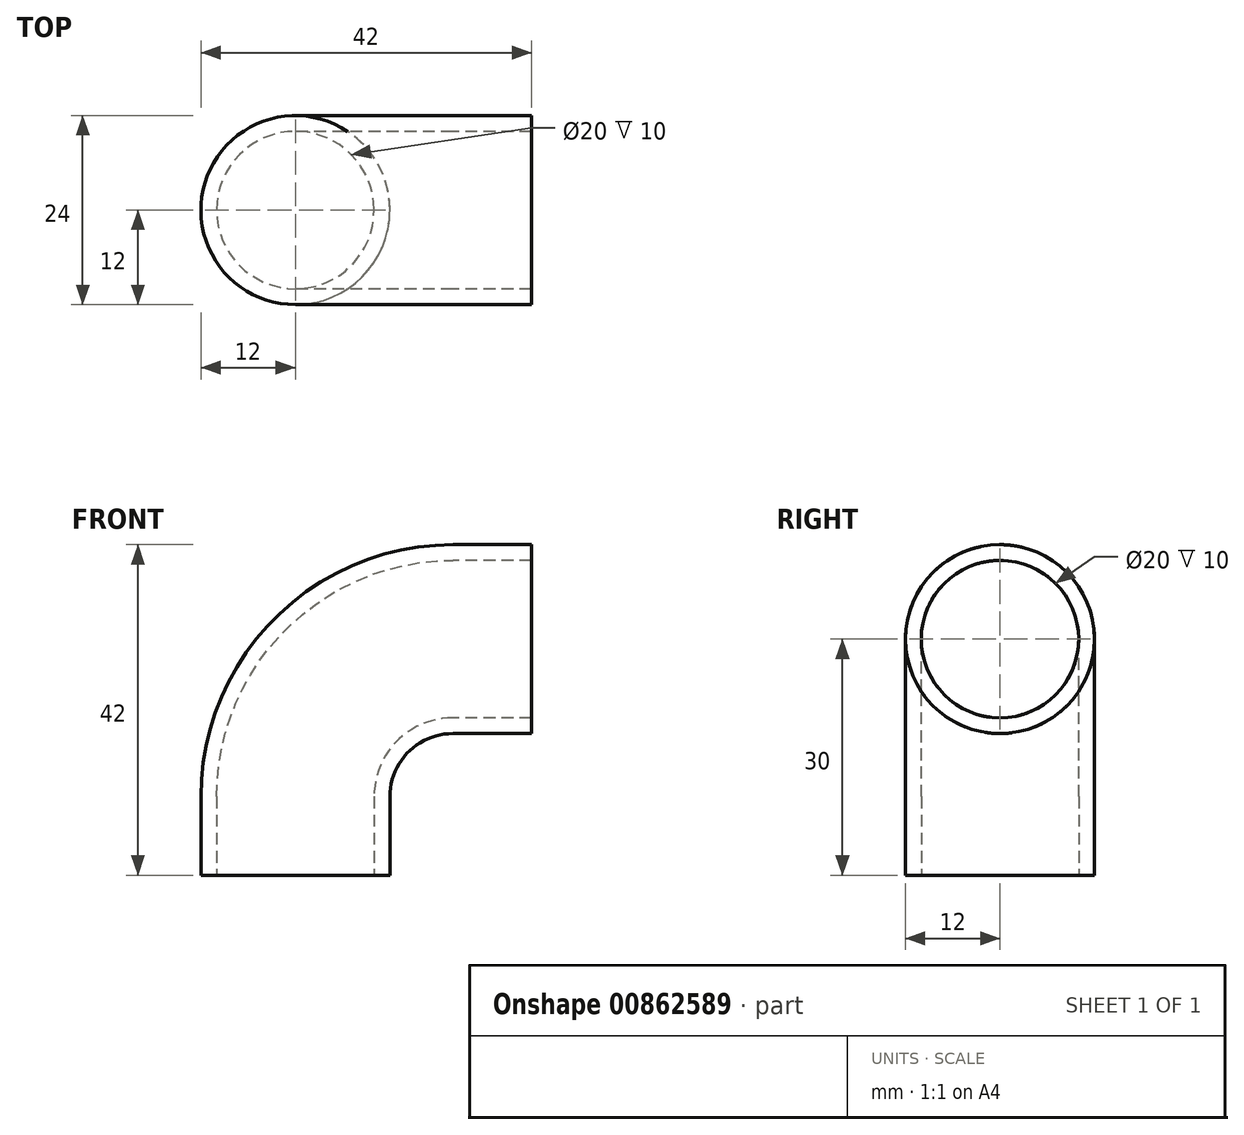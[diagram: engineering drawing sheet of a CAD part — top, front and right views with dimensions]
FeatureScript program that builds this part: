
annotation { "Feature Type Name" : "Feature", "Feature Type Description" : "" }
export const myFeature = defineFeature(function(context is Context, id is Id, definition is map)
    precondition{}
    {
        {
            var Q0;
            Q0=qCreatedBy(makeId("Front.planeOp"),FACE);
            var sketch = newSketch(context, id + "F0", { "sketchPlane" : qUnion([Q0])});
            skLineSegment(sketch, "E0", {"start": v(0, 0) * mm, "end": v(-10, 0) * mm});
            skLineSegment(sketch, "E1", {"start": v(-30, -30) * mm, "end": v(-30, -20) * mm});
            skArc(sketch, "E2", {"start": v(-10, 0) * mm, "mid": v(-24.14, -5.86) * mm, "end": v(-30, -20) * mm});
            skSolve(sketch);
        }
        {
            var Q0;
            Q0=qCreatedBy(makeId("Right.planeOp"),FACE);
            var sketch = newSketch(context, id + "F1", { "sketchPlane" : qUnion([Q0])});
            skCircle(sketch, "E3", {"center": v(0, 0) * mm, "radius": 12 * mm});
            skCircle(sketch, "E4.0", {"center": v(0, 0) * mm, "radius": 10 * mm});
            skSolve(sketch);
        }
        {
            var Q0;
            Q0=makeQuery(id+"F1.imprint","IMPRINT",FACE,{"disambiguationData":[TD([[makeQuery(id+"F1.imprint","IMPRINT",EDGE,{"derivedFrom":sQuery(id+"F1.wireOp",EDGE,"E3")}),1.0]])]});
            var Q1;
            Q1 = qSketchRegion(id + "F0", true);
            var Q2;
            Q2=sQuery(id+"F0.wireOp",EDGE,"E0");
            var Q3;
            Q3=sQuery(id+"F0.wireOp",EDGE,"E2");
            var Q4;
            Q4=sQuery(id+"F0.wireOp",EDGE,"E1");
            sweep(context, id + "F2", {"profiles" : qUnion([Q0, Q1]), "path" : qUnion([Q2, Q3, Q4])});
        }
    });
